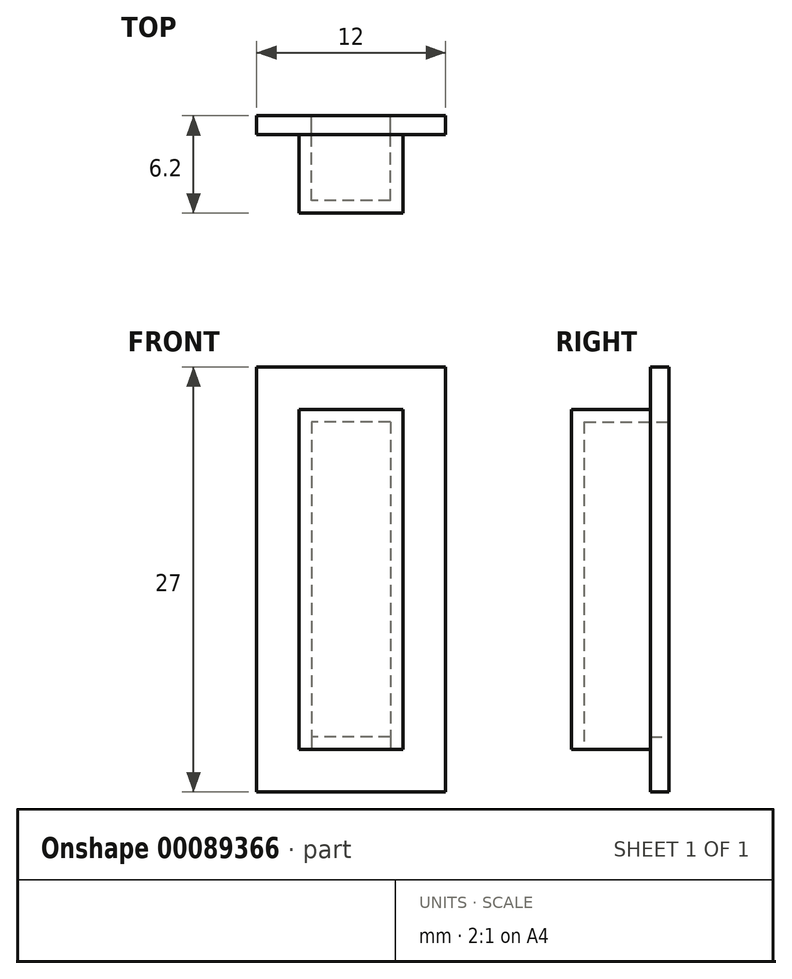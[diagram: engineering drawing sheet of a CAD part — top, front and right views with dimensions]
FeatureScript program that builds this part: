
annotation { "Feature Type Name" : "Feature", "Feature Type Description" : "" }
export const myFeature = defineFeature(function(context is Context, id is Id, definition is map)
    precondition{}
    {
        {
            var Q0;
            Q0=qCreatedBy(makeId("Front.planeOp"),FACE);
            var sketch = newSketch(context, id + "F0", { "sketchPlane" : qUnion([Q0])});
            skLineSegment(sketch, "E0.bottom", {"start": v(6, -13.5) * mm, "end": v(-6, -13.5) * mm});
            skLineSegment(sketch, "E0.top", {"start": v(6, 13.5) * mm, "end": v(-6, 13.5) * mm});
            skLineSegment(sketch, "E0.left", {"start": v(6, -13.5) * mm, "end": v(6, 13.5) * mm});
            skLineSegment(sketch, "E0.right", {"start": v(-6, -13.5) * mm, "end": v(-6, 13.5) * mm});
            skPoint(sketch, "E0.middle", {"position": v(0, 0) * mm});
            skLineSegment(sketch, "E1.bottom", {"start": v(2.5, 10) * mm, "end": v(-2.5, 10) * mm});
            skLineSegment(sketch, "E1.top", {"start": v(2.5, -10) * mm, "end": v(-2.5, -10) * mm});
            skLineSegment(sketch, "E1.left", {"start": v(2.5, 10) * mm, "end": v(2.5, -10) * mm});
            skLineSegment(sketch, "E1.right", {"start": v(-2.5, 10) * mm, "end": v(-2.5, -10) * mm});
            skSolve(sketch);
        }
        {
            var Q0;
            Q0 = qSketchRegion(id + "F0", true);
            extrude(context, id + "F1", {"entities" : qUnion([Q0]), "depth" : 1.2 * mm});
        }
        {
            var Q0;
            Q0=makeQuery(id+"F1.opExtrude","CAP_FACE",FACE,{"disambiguationData":[OSD([sQuery(id+"F0.wireOp",EDGE,"E0.bottom"),sQuery(id+"F0.wireOp",EDGE,"E0.top"),sQuery(id+"F0.wireOp",EDGE,"E0.left"),sQuery(id+"F0.wireOp",EDGE,"E0.right"),sQuery(id+"F0.wireOp",EDGE,"E1.bottom"),sQuery(id+"F0.wireOp",EDGE,"E1.top"),sQuery(id+"F0.wireOp",EDGE,"E1.left"),sQuery(id+"F0.wireOp",EDGE,"E1.right")])],"isStart":false});
            var sketch = newSketch(context, id + "F2", { "sketchPlane" : qUnion([Q0])});
            skLineSegment(sketch, "E2.bottom", {"start": v(-2.5, 10) * mm, "end": v(2.5, 10) * mm});
            skLineSegment(sketch, "E2.left", {"start": v(-2.5, 10) * mm, "end": v(-2.5, -10.8) * mm});
            skLineSegment(sketch, "E2.right", {"start": v(2.5, 10) * mm, "end": v(2.5, -10.8) * mm});
            skLineSegment(sketch, "E3.bottom", {"start": v(3.3, 10.8) * mm, "end": v(-3.3, 10.8) * mm});
            skLineSegment(sketch, "E3.top", {"start": v(3.3, -10.8) * mm, "end": v(2.5, -10.8) * mm});
            skLineSegment(sketch, "E3.left", {"start": v(3.3, 10.8) * mm, "end": v(3.3, -10.8) * mm});
            skLineSegment(sketch, "E3.right", {"start": v(-3.3, 10.8) * mm, "end": v(-3.3, -10.8) * mm});
            skPoint(sketch, "E3.middle", {"position": v(0, 0) * mm});
            skLineSegment(sketch, "E4", {"start": v(-2.5, -10.8) * mm, "end": v(-2.5, -10.8) * mm});
            skLineSegment(sketch, "E5", {"start": v(-2.5, -10.8) * mm, "end": v(-3.3, -10.8) * mm});
            skLineSegment(sketch, "E6", {"start": v(2.5, -10) * mm, "end": v(2.5, -10.8) * mm});
            skSolve(sketch);
        }
        {
            var Q0;
            Q0 = qSketchRegion(id + "F2", true);
            extrude(context, id + "F3", {"entities" : qUnion([Q0]), "operationType" : NewBodyOperationType.ADD, "depth" : 4.2 * mm});
        }
        {
            var Q0;
            Q0=makeQuery(id+"F3.opExtrude","CAP_FACE",FACE,{"disambiguationData":[OSD([sQuery(id+"F2.wireOp",EDGE,"E2.bottom"),sQuery(id+"F2.wireOp",EDGE,"E2.left"),sQuery(id+"F2.wireOp",EDGE,"E2.right"),sQuery(id+"F2.wireOp",EDGE,"E3.bottom"),sQuery(id+"F2.wireOp",EDGE,"E3.top"),sQuery(id+"F2.wireOp",EDGE,"E3.left"),sQuery(id+"F2.wireOp",EDGE,"E3.right"),sQuery(id+"F2.wireOp",EDGE,"E5"),sQuery(id+"F2.wireOp",EDGE,"E6")])],"isStart":false});
            var sketch = newSketch(context, id + "F4", { "sketchPlane" : qUnion([Q0])});
            skLineSegment(sketch, "E7.bottom", {"start": v(-3.3, 10.8) * mm, "end": v(3.3, 10.8) * mm});
            skLineSegment(sketch, "E7.top", {"start": v(-3.3, -10.8) * mm, "end": v(3.3, -10.8) * mm});
            skLineSegment(sketch, "E7.left", {"start": v(-3.3, 10.8) * mm, "end": v(-3.3, -10.8) * mm});
            skLineSegment(sketch, "E7.right", {"start": v(3.3, 10.8) * mm, "end": v(3.3, -10.8) * mm});
            skSolve(sketch);
        }
        {
            var Q0;
            Q0 = qSketchRegion(id + "F4", true);
            extrude(context, id + "F5", {"entities" : qUnion([Q0]), "operationType" : NewBodyOperationType.ADD, "depth" : 0.8 * mm});
        }
    });
